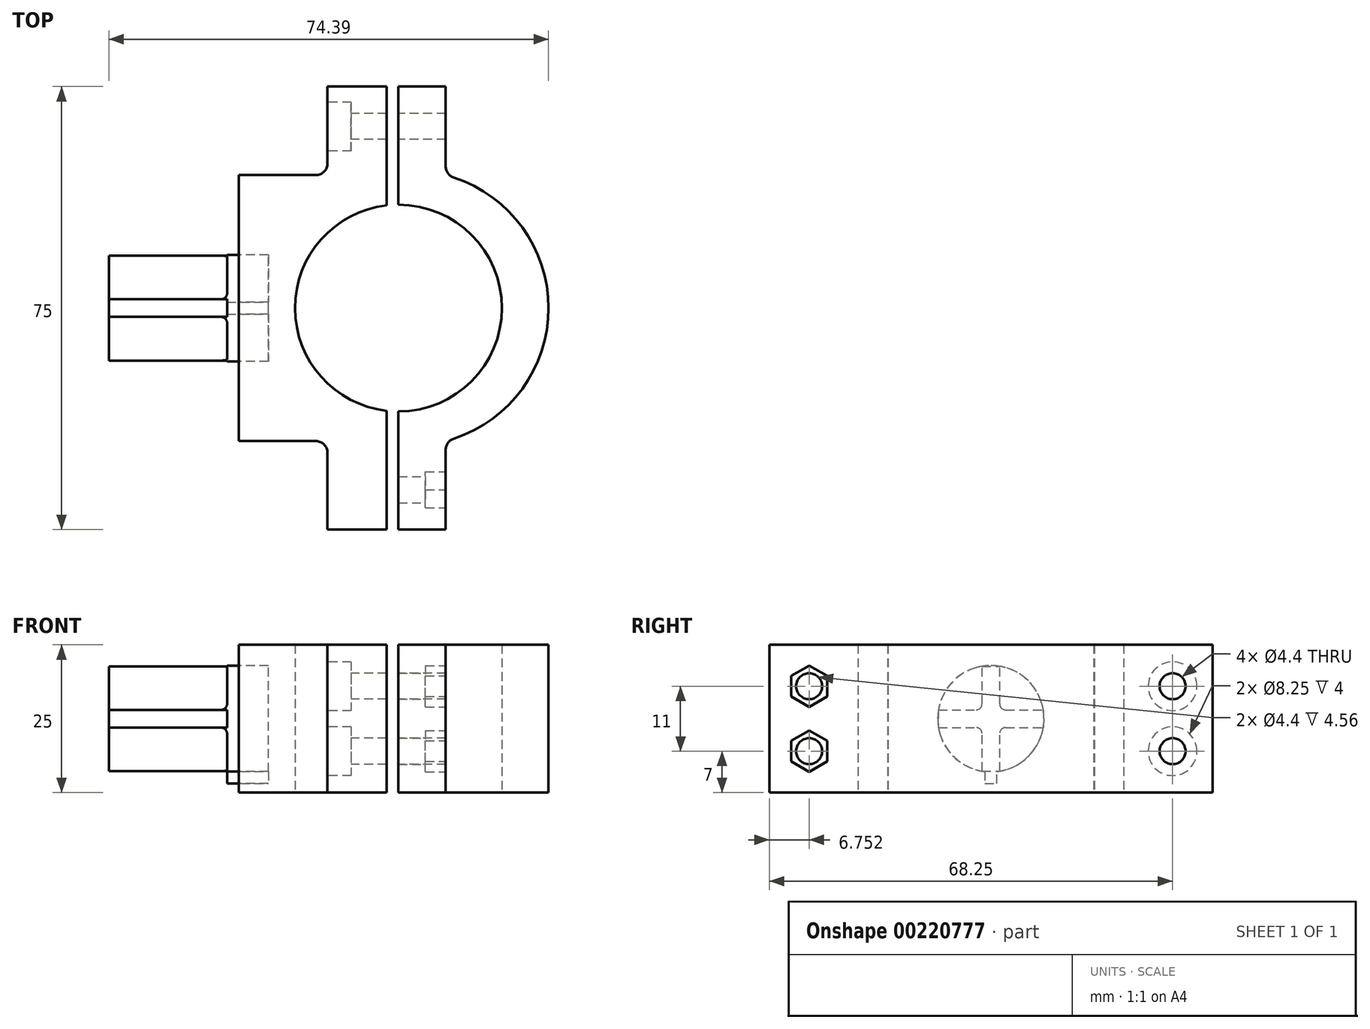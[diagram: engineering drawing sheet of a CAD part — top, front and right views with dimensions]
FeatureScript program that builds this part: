
annotation { "Feature Type Name" : "Feature", "Feature Type Description" : "" }
export const myFeature = defineFeature(function(context is Context, id is Id, definition is map)
    precondition{}
    {
        {
            var Q0;
            Q0=qCreatedBy(makeId("Top.planeOp"),FACE);
            var sketch = newSketch(context, id + "F0", { "sketchPlane" : qUnion([Q0])});
            skCircle(sketch, "E0", {"center": v(0, 0) * mm, "radius": 17.5 * mm, "construction": true});
            skLineSegment(sketch, "E1", {"start": v(0, 37.5) * mm, "end": v(0, 17.5) * mm});
            skLineSegment(sketch, "E2", {"start": v(0, -37.5) * mm, "end": v(0, -17.5) * mm});
            skArc(sketch, "E3", {"start": v(0, -17.5) * mm, "mid": v(17.5, 0) * mm, "end": v(0, 17.5) * mm});
            skLineSegment(sketch, "E4", {"start": v(0, -37.5) * mm, "end": v(8, -37.5) * mm});
            skLineSegment(sketch, "E5", {"start": v(8, -37.5) * mm, "end": v(8, -24) * mm});
            skLineSegment(sketch, "E6", {"start": v(0, 37.5) * mm, "end": v(8, 37.5) * mm});
            skLineSegment(sketch, "E7", {"start": v(8, 37.5) * mm, "end": v(8, 24) * mm});
            skArc(sketch, "E8", {"start": v(9.38, -22.1) * mm, "mid": v(25.4, 0) * mm, "end": v(9.38, 22.1) * mm});
            skPoint(sketch, "E9.visualSharp", {"position": v(8, -22.5) * mm});
            skArc(sketch, "E9.filletArc", {"start": v(9.38, -22.1) * mm, "mid": v(8.38, -22.82) * mm, "end": v(8, -24) * mm});
            skPoint(sketch, "E10.visualSharp", {"position": v(8, 22.5) * mm});
            skArc(sketch, "E10.filletArc", {"start": v(8, 24) * mm, "mid": v(8.38, 22.82) * mm, "end": v(9.38, 22.1) * mm});
            skSolve(sketch);
        }
        {
            var Q0;
            Q0=makeQuery(id+"F0.imprint","IMPRINT",FACE,{"disambiguationData":[TD([[makeQuery(id+"F0.imprint","IMPRINT",EDGE,{"derivedFrom":sQuery(id+"F0.wireOp",EDGE,"E1")}),1.0]])]});
            extrude(context, id + "F1", {"entities" : qUnion([Q0]), "depth" : 25 * mm});
        }
        {
            var Q0;
            Q0=makeQuery(id+"F1.opExtrude","SWEPT_FACE",FACE,{"disambiguationData":[OSD([sQuery(id+"F0.wireOp",EDGE,"E5")])]});
            var sketch = newSketch(context, id + "F2", { "sketchPlane" : qUnion([Q0])});
            skCircle(sketch, "E11.cCircle", {"center": v(-30.75, 18) * mm, "radius": 3.03 * mm, "construction": true});
            skLineSegment(sketch, "E11.0", {"start": v(-30.75, 21.5) * mm, "end": v(-27.72, 19.75) * mm});
            skLineSegment(sketch, "E11.1", {"start": v(-27.72, 19.75) * mm, "end": v(-27.72, 16.25) * mm});
            skLineSegment(sketch, "E11.2", {"start": v(-27.72, 16.25) * mm, "end": v(-30.75, 14.5) * mm});
            skLineSegment(sketch, "E11.3", {"start": v(-30.75, 14.5) * mm, "end": v(-33.78, 16.25) * mm});
            skLineSegment(sketch, "E11.4", {"start": v(-33.78, 16.25) * mm, "end": v(-33.78, 19.75) * mm});
            skLineSegment(sketch, "E11.5", {"start": v(-33.78, 19.75) * mm, "end": v(-30.75, 21.5) * mm});
            skPoint(sketch, "E11.0.midPoint", {"position": v(-29.23, 20.63) * mm});
            skLineSegment(sketch, "E12", {"start": v(-37.5, 7) * mm, "end": v(-24, 7) * mm, "construction": true});
            skLineSegment(sketch, "E13", {"start": v(-24, 18) * mm, "end": v(-37.5, 18) * mm, "construction": true});
            skLineSegment(sketch, "E14", {"start": v(-30.75, 18) * mm, "end": v(-30.75, 25) * mm, "construction": true});
            skLineSegment(sketch, "E15", {"start": v(-30.75, 7) * mm, "end": v(-30.75, 0) * mm, "construction": true});
            skCircle(sketch, "E16.cCircle", {"center": v(-30.75, 7) * mm, "radius": 3.03 * mm, "construction": true});
            skLineSegment(sketch, "E16.0", {"start": v(-30.75, 10.5) * mm, "end": v(-27.72, 8.75) * mm});
            skLineSegment(sketch, "E16.1", {"start": v(-27.72, 8.75) * mm, "end": v(-27.72, 5.25) * mm});
            skLineSegment(sketch, "E16.2", {"start": v(-27.72, 5.25) * mm, "end": v(-30.75, 3.5) * mm});
            skLineSegment(sketch, "E16.3", {"start": v(-30.75, 3.5) * mm, "end": v(-33.78, 5.25) * mm});
            skLineSegment(sketch, "E16.4", {"start": v(-33.78, 5.25) * mm, "end": v(-33.78, 8.75) * mm});
            skLineSegment(sketch, "E16.5", {"start": v(-33.78, 8.75) * mm, "end": v(-30.75, 10.5) * mm});
            skPoint(sketch, "E16.0.midPoint", {"position": v(-29.23, 9.62) * mm});
            skSolve(sketch);
        }
        {
            var Q0;
            Q0 = qSketchRegion(id + "F2", true);
            extrude(context, id + "F3", {"entities" : qUnion([Q0]), "operationType" : NewBodyOperationType.REMOVE, "oppositeDirection" : true, "depth" : 3.44 * mm});
        }
        {
            var Q0;
            Q0=makeQuery(id+"F3.boolean.opBoolean","COPY",FACE,{"derivedFrom":makeQuery(id+"F3.opExtrude","CAP_FACE",FACE,{"disambiguationData":[OSD([sQuery(id+"F2.wireOp",EDGE,"E11.0"),sQuery(id+"F2.wireOp",EDGE,"E11.1"),sQuery(id+"F2.wireOp",EDGE,"E11.2"),sQuery(id+"F2.wireOp",EDGE,"E11.3"),sQuery(id+"F2.wireOp",EDGE,"E11.4"),sQuery(id+"F2.wireOp",EDGE,"E11.5")])],"isStart":false})});
            var sketch = newSketch(context, id + "F4", { "sketchPlane" : qUnion([Q0])});
            skLineSegment(sketch, "E17", {"start": v(-33.78, 19.75) * mm, "end": v(-27.72, 16.25) * mm, "construction": true});
            skLineSegment(sketch, "E18", {"start": v(-27.72, 16.25) * mm, "end": v(-30.75, 21.5) * mm, "construction": true});
            skLineSegment(sketch, "E19", {"start": v(-30.75, 21.5) * mm, "end": v(-30.75, 14.5) * mm, "construction": true});
            skPoint(sketch, "E20", {"position": v(-30.75, 18) * mm});
            skSolve(sketch);
        }
        {
            var Q0;
            Q0=sQuery(id+"F4.wireOp",VERTEX,"E20");
            var Q1;
            Q1=makeQuery(id+"F1.opExtrude","SWEPT_BODY",BODY,{"disambiguationData":[OSD([sQuery(id+"F0.wireOp",EDGE,"E1"),sQuery(id+"F0.wireOp",EDGE,"E2"),sQuery(id+"F0.wireOp",EDGE,"E3"),sQuery(id+"F0.wireOp",EDGE,"E4"),sQuery(id+"F0.wireOp",EDGE,"E5"),sQuery(id+"F0.wireOp",EDGE,"E6"),sQuery(id+"F0.wireOp",EDGE,"E7"),sQuery(id+"F0.wireOp",EDGE,"E8"),sQuery(id+"F0.wireOp",EDGE,"E9.filletArc"),sQuery(id+"F0.wireOp",EDGE,"E10.filletArc")])]});
            hole(context, id + "F5", {"style" : HoleStyle.SIMPLE, "endStyle" : HoleEndStyle.THROUGH, "standardTappedOrClearance" : lookupTablePath({ "standard" : "ISO", "fit" : "Normal", "size" : "M4", "type" : "Clearance" }), "standardBlindInLast" : lookupTablePath({ "fit" : "Standard", "standard" : "ISO", "size" : "M4", "type" : "Clearance" }), "holeDiameter" : 4.4 * mm, "startFromSketch" : true, "locations" : qUnion([Q0]), "scope" : qUnion([Q1]), "isTappedThrough" : true});
        }
        {
            var Q0;
            Q0=makeQuery(id+"F3.boolean.opBoolean","COPY",FACE,{"derivedFrom":makeQuery(id+"F3.opExtrude","CAP_FACE",FACE,{"disambiguationData":[OSD([sQuery(id+"F2.wireOp",EDGE,"E16.0"),sQuery(id+"F2.wireOp",EDGE,"E16.1"),sQuery(id+"F2.wireOp",EDGE,"E16.2"),sQuery(id+"F2.wireOp",EDGE,"E16.3"),sQuery(id+"F2.wireOp",EDGE,"E16.4"),sQuery(id+"F2.wireOp",EDGE,"E16.5")])],"isStart":false})});
            var sketch = newSketch(context, id + "F6", { "sketchPlane" : qUnion([Q0])});
            skLineSegment(sketch, "E21", {"start": v(-33.78, 8.75) * mm, "end": v(-27.72, 5.25) * mm, "construction": true});
            skLineSegment(sketch, "E22", {"start": v(-27.72, 5.25) * mm, "end": v(-30.75, 10.5) * mm, "construction": true});
            skLineSegment(sketch, "E23", {"start": v(-30.75, 10.5) * mm, "end": v(-30.75, 3.5) * mm, "construction": true});
            skPoint(sketch, "E24", {"position": v(-30.75, 7) * mm});
            skSolve(sketch);
        }
        {
            var Q0;
            Q0=sQuery(id+"F6.wireOp",VERTEX,"E24");
            var Q1;
            Q1=makeQuery(id+"F1.opExtrude","SWEPT_BODY",BODY,{"disambiguationData":[OSD([sQuery(id+"F0.wireOp",EDGE,"E1"),sQuery(id+"F0.wireOp",EDGE,"E2"),sQuery(id+"F0.wireOp",EDGE,"E3"),sQuery(id+"F0.wireOp",EDGE,"E4"),sQuery(id+"F0.wireOp",EDGE,"E5"),sQuery(id+"F0.wireOp",EDGE,"E6"),sQuery(id+"F0.wireOp",EDGE,"E7"),sQuery(id+"F0.wireOp",EDGE,"E8"),sQuery(id+"F0.wireOp",EDGE,"E9.filletArc"),sQuery(id+"F0.wireOp",EDGE,"E10.filletArc")])]});
            hole(context, id + "F7", {"style" : HoleStyle.SIMPLE, "endStyle" : HoleEndStyle.THROUGH, "standardTappedOrClearance" : lookupTablePath({ "standard" : "ISO", "fit" : "Normal", "size" : "M4", "type" : "Clearance" }), "standardBlindInLast" : lookupTablePath({ "fit" : "Standard", "standard" : "ISO", "size" : "M4", "type" : "Clearance" }), "holeDiameter" : 4.4 * mm, "startFromSketch" : true, "locations" : qUnion([Q0]), "scope" : qUnion([Q1]), "isTappedThrough" : true});
        }
        {
            var Q0;
            Q0=qCreatedBy(makeId("Top.planeOp"),FACE);
            var sketch = newSketch(context, id + "F8", { "sketchPlane" : qUnion([Q0])});
            skCircle(sketch, "E25", {"center": v(0, 0) * mm, "radius": 17.5 * mm, "construction": true});
            skLineSegment(sketch, "E26", {"start": v(0, 17.5) * mm, "end": v(0, 37.5) * mm});
            skLineSegment(sketch, "E27", {"start": v(0, 37.5) * mm, "end": v(-12, 37.5) * mm});
            skLineSegment(sketch, "E28", {"start": v(0, -17.5) * mm, "end": v(0, -37.5) * mm});
            skLineSegment(sketch, "E29", {"start": v(0, -37.5) * mm, "end": v(-12, -37.5) * mm});
            skLineSegment(sketch, "E30", {"start": v(-12, 37.5) * mm, "end": v(-12, 24.5) * mm});
            skLineSegment(sketch, "E31", {"start": v(-12, -37.5) * mm, "end": v(-12, -24.5) * mm});
            skLineSegment(sketch, "E32", {"start": v(-14, 22.5) * mm, "end": v(-27, 22.5) * mm});
            skLineSegment(sketch, "E33", {"start": v(-14, -22.5) * mm, "end": v(-27, -22.5) * mm});
            skArc(sketch, "E34", {"start": v(0, 17.5) * mm, "mid": v(-17.5, 0) * mm, "end": v(0, -17.5) * mm});
            skLineSegment(sketch, "E35", {"start": v(-27, 22.5) * mm, "end": v(-27, -22.5) * mm});
            skPoint(sketch, "E36.visualSharp", {"position": v(-12, 22.5) * mm});
            skArc(sketch, "E36.filletArc", {"start": v(-14, 22.5) * mm, "mid": v(-12.59, 23.09) * mm, "end": v(-12, 24.5) * mm});
            skPoint(sketch, "E37.visualSharp", {"position": v(-12, -22.5) * mm});
            skArc(sketch, "E37.filletArc", {"start": v(-12, -24.5) * mm, "mid": v(-12.59, -23.09) * mm, "end": v(-14, -22.5) * mm});
            skSolve(sketch);
        }
        {
            var Q0;
            Q0=makeQuery(id+"F8.imprint","IMPRINT",FACE,{"disambiguationData":[TD([[makeQuery(id+"F8.imprint","IMPRINT",EDGE,{"derivedFrom":sQuery(id+"F8.wireOp",EDGE,"E26")}),1.0]])]});
            extrude(context, id + "F9", {"entities" : qUnion([Q0]), "depth" : 25 * mm});
        }
        {
            var Q0;
            Q0=makeQuery(id+"F9.opExtrude","SWEPT_FACE",FACE,{"disambiguationData":[OSD([sQuery(id+"F8.wireOp",EDGE,"E30")])]});
            var sketch = newSketch(context, id + "F10", { "sketchPlane" : qUnion([Q0])});
            skLineSegment(sketch, "E38", {"start": v(-30.75, 25) * mm, "end": v(-30.75, 0) * mm, "construction": true});
            skLineSegment(sketch, "E39", {"start": v(-30.75, 18) * mm, "end": v(-37.5, 18) * mm, "construction": true});
            skLineSegment(sketch, "E40", {"start": v(-30.75, 7) * mm, "end": v(-37.5, 7) * mm, "construction": true});
            skPoint(sketch, "E41", {"position": v(-30.75, 18) * mm});
            skPoint(sketch, "E42", {"position": v(-30.75, 7) * mm});
            skSolve(sketch);
        }
        {
            var Q0;
            Q0=sQuery(id+"F10.wireOp",VERTEX,"E41");
            var Q1;
            Q1=sQuery(id+"F10.wireOp",VERTEX,"E42");
            var Q2;
            Q2=makeQuery(id+"F1.opExtrude","SWEPT_BODY",BODY,{"disambiguationData":[OSD([sQuery(id+"F0.wireOp",EDGE,"E1"),sQuery(id+"F0.wireOp",EDGE,"E2"),sQuery(id+"F0.wireOp",EDGE,"E3"),sQuery(id+"F0.wireOp",EDGE,"E4"),sQuery(id+"F0.wireOp",EDGE,"E5"),sQuery(id+"F0.wireOp",EDGE,"E6"),sQuery(id+"F0.wireOp",EDGE,"E7"),sQuery(id+"F0.wireOp",EDGE,"E8"),sQuery(id+"F0.wireOp",EDGE,"E9.filletArc"),sQuery(id+"F0.wireOp",EDGE,"E10.filletArc")])]});
            var Q3;
            Q3=makeQuery(id+"F9.opExtrude","SWEPT_BODY",BODY,{"disambiguationData":[OSD([sQuery(id+"F8.wireOp",EDGE,"E26"),sQuery(id+"F8.wireOp",EDGE,"E27"),sQuery(id+"F8.wireOp",EDGE,"E28"),sQuery(id+"F8.wireOp",EDGE,"E29"),sQuery(id+"F8.wireOp",EDGE,"E30"),sQuery(id+"F8.wireOp",EDGE,"E31"),sQuery(id+"F8.wireOp",EDGE,"E32"),sQuery(id+"F8.wireOp",EDGE,"E33"),sQuery(id+"F8.wireOp",EDGE,"E34"),sQuery(id+"F8.wireOp",EDGE,"E35"),sQuery(id+"F8.wireOp",EDGE,"E36.filletArc"),sQuery(id+"F8.wireOp",EDGE,"E37.filletArc")])]});
            hole(context, id + "F11", {"style" : HoleStyle.C_BORE, "endStyle" : HoleEndStyle.THROUGH, "standardTappedOrClearance" : lookupTablePath({ "standard" : "ISO", "fit" : "Normal", "size" : "M4", "type" : "Clearance" }), "standardBlindInLast" : lookupTablePath({ "fit" : "Standard", "standard" : "ISO", "size" : "M4", "type" : "Clearance" }), "holeDiameter" : 4.4 * mm, "cBoreDiameter" : 8.25 * mm, "cBoreDepth" : 4 * mm, "startFromSketch" : true, "locations" : qUnion([Q0, Q1]), "scope" : qUnion([Q2, Q3]), "isTappedThrough" : true});
        }
        {
            var Q0;
            Q0=makeQuery(id+"F9.opExtrude","SWEPT_FACE",FACE,{"disambiguationData":[OSD([sQuery(id+"F8.wireOp",EDGE,"E35")])]});
            var sketch = newSketch(context, id + "F12", { "sketchPlane" : qUnion([Q0])});
            skLineSegment(sketch, "E43", {"start": v(0, 25) * mm, "end": v(0, 0) * mm, "construction": true});
            skLineSegment(sketch, "E44", {"start": v(22.5, 12.5) * mm, "end": v(0, 12.5) * mm, "construction": true});
            skArc(sketch, "E45", {"start": v(1, 3.56) * mm, "mid": v(0, 21.5) * mm, "end": v(-1, 3.56) * mm});
            skLineSegment(sketch, "E46", {"start": v(1, 3.56) * mm, "end": v(1, 1.56) * mm});
            skLineSegment(sketch, "E47", {"start": v(1, 1.56) * mm, "end": v(-1, 1.56) * mm});
            skLineSegment(sketch, "E48", {"start": v(-1, 1.56) * mm, "end": v(-1, 3.56) * mm});
            skSolve(sketch);
        }
        {
            var Q0;
            Q0=makeQuery(id+"F12.imprint","IMPRINT",FACE,{"disambiguationData":[TD([[makeQuery(id+"F12.imprint","IMPRINT",EDGE,{"derivedFrom":sQuery(id+"F12.wireOp",EDGE,"E45")}),1.0]])]});
            extrude(context, id + "F13", {"entities" : qUnion([Q0]), "operationType" : NewBodyOperationType.REMOVE, "oppositeDirection" : true, "depth" : 5 * mm});
        }
        {
            var Q0;
            Q0=makeQuery(id+"F13.boolean.opBoolean","COPY",FACE,{"derivedFrom":makeQuery(id+"F13.opExtrude","CAP_FACE",FACE,{"disambiguationData":[OSD([sQuery(id+"F12.wireOp",EDGE,"E45"),sQuery(id+"F12.wireOp",EDGE,"E46"),sQuery(id+"F12.wireOp",EDGE,"E47"),sQuery(id+"F12.wireOp",EDGE,"E48")])],"isStart":false})});
            extrude(context, id + "F14", {"entities" : qUnion([Q0]), "depth" : 7 * mm});
        }
        {
            var Q0;
            Q0=makeQuery(id+"F14.opExtrude","CAP_FACE",FACE,{"disambiguationData":[OSD([sQuery(id+"F12.wireOp",EDGE,"E45"),sQuery(id+"F12.wireOp",EDGE,"E46"),sQuery(id+"F12.wireOp",EDGE,"E47"),sQuery(id+"F12.wireOp",EDGE,"E48")])],"isStart":false});
            var sketch = newSketch(context, id + "F15", { "sketchPlane" : qUnion([Q0])});
            skLineSegment(sketch, "E49", {"start": v(0, 12.5) * mm, "end": v(9, 12.5) * mm, "construction": true});
            skLineSegment(sketch, "E50", {"start": v(9, 12.5) * mm, "end": v(0, 21.5) * mm, "construction": true});
            skLineSegment(sketch, "E51", {"start": v(0, 21.5) * mm, "end": v(0, 1.56) * mm, "construction": true});
            skLineSegment(sketch, "E52.bottom", {"start": v(8.87, 14) * mm, "end": v(2.5, 14) * mm});
            skLineSegment(sketch, "E52.top", {"start": v(8.87, 11) * mm, "end": v(2.5, 11) * mm});
            skLineSegment(sketch, "E52.left", {"start": v(8.87, 14) * mm, "end": v(8.87, 11) * mm});
            skLineSegment(sketch, "E52.right", {"start": v(-8.87, 14) * mm, "end": v(-8.87, 11) * mm});
            skPoint(sketch, "E52.middle", {"position": v(0, 12.5) * mm});
            skLineSegment(sketch, "E53.bottom", {"start": v(1.5, 3.63) * mm, "end": v(-1.5, 3.63) * mm});
            skLineSegment(sketch, "E53.top", {"start": v(1.5, 21.37) * mm, "end": v(-1.5, 21.37) * mm});
            skLineSegment(sketch, "E53.left", {"start": v(1.5, 3.63) * mm, "end": v(1.5, 10) * mm});
            skLineSegment(sketch, "E53.right", {"start": v(-1.5, 3.63) * mm, "end": v(-1.5, 10) * mm});
            skLineSegment(sketch, "E54.trimOffspring", {"start": v(-1.5, 15) * mm, "end": v(-1.5, 21.37) * mm});
            skLineSegment(sketch, "E55.trimOffspring", {"start": v(-2.5, 14) * mm, "end": v(-8.87, 14) * mm});
            skLineSegment(sketch, "E56.trimOffspring", {"start": v(1.5, 15) * mm, "end": v(1.5, 21.37) * mm});
            skLineSegment(sketch, "E57.trimOffspring", {"start": v(-2.5, 11) * mm, "end": v(-8.87, 11) * mm});
            skPoint(sketch, "E58.visualSharp", {"position": v(-1.5, 14) * mm});
            skArc(sketch, "E58.filletArc", {"start": v(-2.5, 14) * mm, "mid": v(-1.8, 14.3) * mm, "end": v(-1.5, 15) * mm});
            skPoint(sketch, "E59.visualSharp", {"position": v(1.5, 14) * mm});
            skArc(sketch, "E59.filletArc", {"start": v(1.5, 15) * mm, "mid": v(1.8, 14.3) * mm, "end": v(2.5, 14) * mm});
            skPoint(sketch, "E60.visualSharp", {"position": v(1.5, 11) * mm});
            skArc(sketch, "E60.filletArc", {"start": v(2.5, 11) * mm, "mid": v(1.8, 10.7) * mm, "end": v(1.5, 10) * mm});
            skPoint(sketch, "E61.visualSharp", {"position": v(-1.5, 11) * mm});
            skArc(sketch, "E61.filletArc", {"start": v(-1.5, 10) * mm, "mid": v(-1.8, 10.7) * mm, "end": v(-2.5, 11) * mm});
            skSolve(sketch);
        }
        {
            var Q0;
            Q0=makeQuery(id+"F15.imprint","IMPRINT",FACE,{"disambiguationData":[TD([[makeQuery(id+"F15.imprint","IMPRINT",EDGE,{"derivedFrom":sQuery(id+"F15.wireOp",EDGE,"E52.bottom")}),1.0]])]});
            extrude(context, id + "F16", {"entities" : qUnion([Q0]), "operationType" : NewBodyOperationType.ADD, "depth" : 20 * mm});
        }
        {
            var Q0;
            Q0=makeQuery(id+"F16.opExtrude","CAP_EDGE",EDGE,{"disambiguationData":[OSD([sQuery(id+"F15.wireOp",EDGE,"E55.trimOffspring")])],"isStart":true});
            var Q1;
            Q1=makeQuery(id+"F16.opExtrude","CAP_EDGE",EDGE,{"disambiguationData":[OSD([sQuery(id+"F15.wireOp",EDGE,"E58.filletArc")])],"isStart":true});
            var Q2;
            Q2=makeQuery(id+"F16.opExtrude","CAP_EDGE",EDGE,{"disambiguationData":[OSD([sQuery(id+"F15.wireOp",EDGE,"E54.trimOffspring")])],"isStart":true});
            var Q3;
            Q3=makeQuery(id+"F16.opExtrude","CAP_EDGE",EDGE,{"disambiguationData":[OSD([sQuery(id+"F15.wireOp",EDGE,"E57.trimOffspring")])],"isStart":true});
            var Q4;
            Q4=makeQuery(id+"F16.opExtrude","CAP_EDGE",EDGE,{"disambiguationData":[OSD([sQuery(id+"F15.wireOp",EDGE,"E53.right")])],"isStart":true});
            var Q5;
            Q5=makeQuery(id+"F16.opExtrude","CAP_EDGE",EDGE,{"disambiguationData":[OSD([sQuery(id+"F15.wireOp",EDGE,"E61.filletArc")])],"isStart":true});
            var Q6;
            Q6=makeQuery(id+"F16.opExtrude","CAP_EDGE",EDGE,{"disambiguationData":[OSD([sQuery(id+"F15.wireOp",EDGE,"E53.left")])],"isStart":true});
            var Q7;
            Q7=makeQuery(id+"F16.opExtrude","CAP_EDGE",EDGE,{"disambiguationData":[OSD([sQuery(id+"F15.wireOp",EDGE,"E52.top")])],"isStart":true});
            var Q8;
            Q8=makeQuery(id+"F16.opExtrude","CAP_EDGE",EDGE,{"disambiguationData":[OSD([sQuery(id+"F15.wireOp",EDGE,"E52.bottom")])],"isStart":true});
            var Q9;
            Q9=makeQuery(id+"F16.opExtrude","CAP_EDGE",EDGE,{"disambiguationData":[OSD([sQuery(id+"F15.wireOp",EDGE,"E59.filletArc")])],"isStart":true});
            var Q10;
            Q10=makeQuery(id+"F16.opExtrude","CAP_EDGE",EDGE,{"disambiguationData":[OSD([sQuery(id+"F15.wireOp",EDGE,"E56.trimOffspring")])],"isStart":true});
            fillet(context, id + "F17", {"entities" : qUnion([Q0, Q1, Q2, Q3, Q4, Q5, Q6, Q7, Q8, Q9, Q10]), "radius" : 1 * mm, "tangentPropagation" : true, "allowEdgeOverflow" : false});
        }
        {
            var Q0;
            Q0=makeQuery(id+"F9.opExtrude","SWEPT_FACE",FACE,{"disambiguationData":[OSD([sQuery(id+"F8.wireOp",EDGE,"E26")])]});
            var sketch = newSketch(context, id + "F18", { "sketchPlane" : qUnion([Q0])});
            skLineSegment(sketch, "E62.bottom", {"start": v(37.5, 0) * mm, "end": v(-37.5, 0) * mm});
            skLineSegment(sketch, "E62.top", {"start": v(37.5, 25) * mm, "end": v(-37.5, 25) * mm});
            skLineSegment(sketch, "E62.left", {"start": v(37.5, 0) * mm, "end": v(37.5, 25) * mm});
            skLineSegment(sketch, "E62.right", {"start": v(-37.5, 0) * mm, "end": v(-37.5, 25) * mm});
            skSolve(sketch);
        }
        {
            var Q0;
            Q0 = qSketchRegion(id + "F18", true);
            extrude(context, id + "F19", {"entities" : qUnion([Q0]), "operationType" : NewBodyOperationType.REMOVE, "oppositeDirection" : true, "depth" : 2 * mm});
        }
    });
